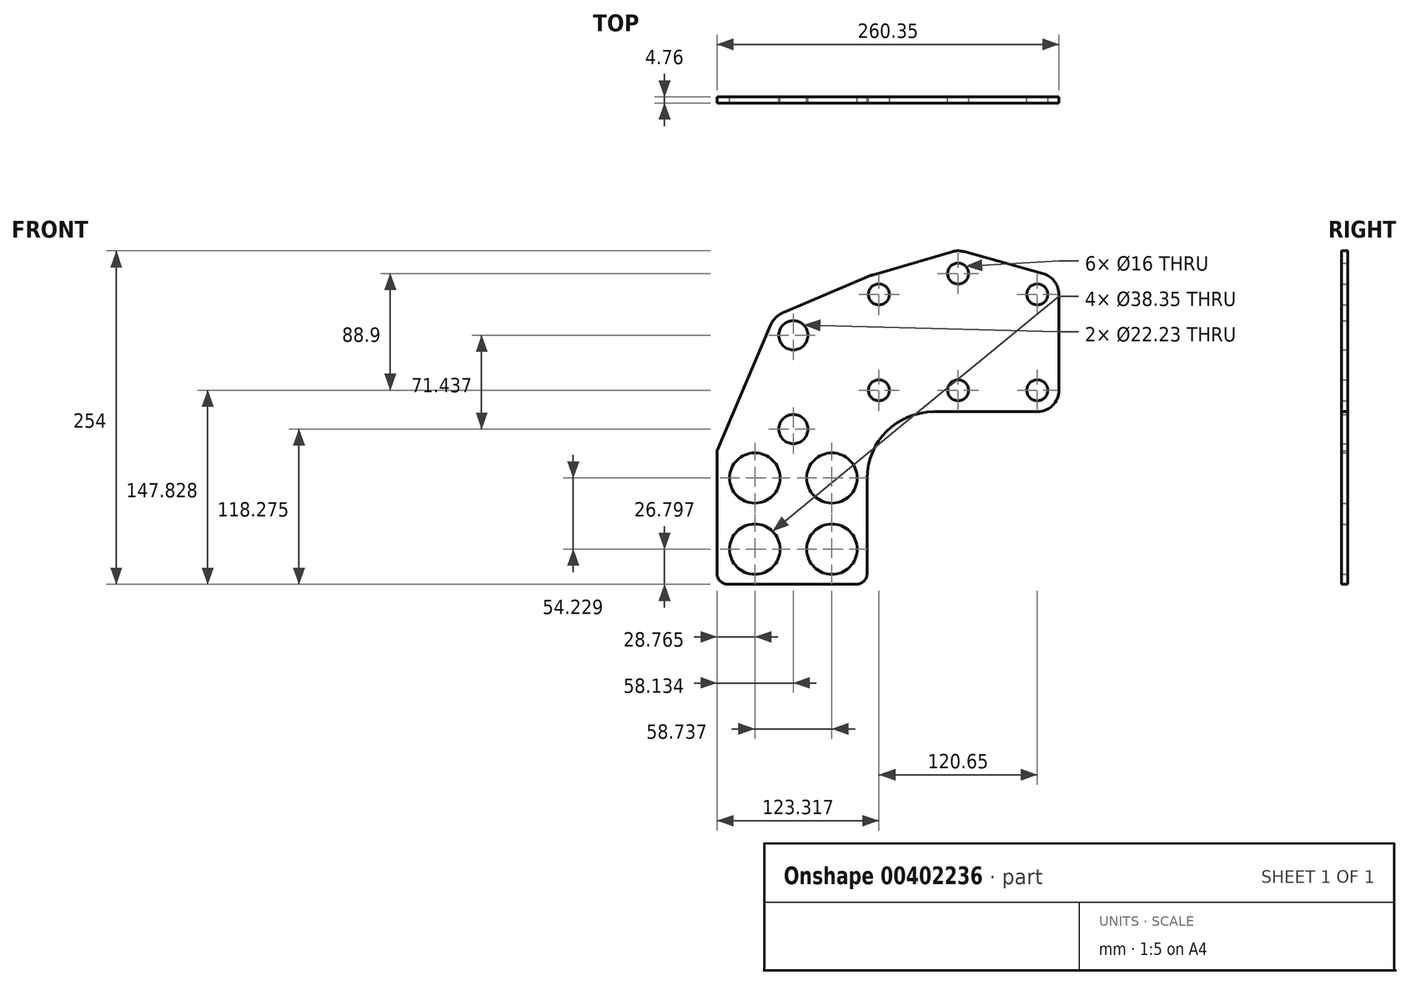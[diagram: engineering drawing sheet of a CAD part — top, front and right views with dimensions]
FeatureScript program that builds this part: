
annotation { "Feature Type Name" : "Feature", "Feature Type Description" : "" }
export const myFeature = defineFeature(function(context is Context, id is Id, definition is map)
    precondition{}
    {
        {
            var Q0;
            Q0=qCreatedBy(makeId("Front.planeOp"),FACE);
            var sketch = newSketch(context, id + "F0", { "sketchPlane" : qUnion([Q0])});
            skLineSegment(sketch, "E0.bottom", {"start": v(8.38, 0) * mm, "end": v(105.92, 0) * mm});
            skLineSegment(sketch, "E0.top", {"start": v(0, 254) * mm, "end": v(183.64, 254) * mm});
            skLineSegment(sketch, "E0.left", {"start": v(0, 8.38) * mm, "end": v(0, 101.6) * mm});
            skLineSegment(sketch, "E0.right", {"start": v(260.35, 0) * mm, "end": v(260.35, 131.45) * mm});
            skLineSegment(sketch, "E1", {"start": v(114.3, 8.38) * mm, "end": v(114.3, 80.64) * mm});
            skLineSegment(sketch, "E2", {"start": v(243.97, 131.45) * mm, "end": v(165.1, 131.45) * mm});
            skCircle(sketch, "E3", {"center": v(28.77, 26.8) * mm, "radius": 19.18 * mm});
            skCircle(sketch, "E4", {"center": v(87.5, 26.8) * mm, "radius": 19.18 * mm});
            skCircle(sketch, "E5", {"center": v(28.77, 81.03) * mm, "radius": 19.18 * mm});
            skCircle(sketch, "E6", {"center": v(87.5, 81.03) * mm, "radius": 19.18 * mm});
            skCircle(sketch, "E7", {"center": v(243.97, 147.83) * mm, "radius": 8 * mm});
            skCircle(sketch, "E8", {"center": v(243.97, 220.85) * mm, "radius": 8 * mm});
            skCircle(sketch, "E9", {"center": v(183.64, 147.83) * mm, "radius": 8 * mm});
            skCircle(sketch, "E10", {"center": v(183.64, 236.73) * mm, "radius": 8 * mm});
            skCircle(sketch, "E11", {"center": v(123.32, 147.83) * mm, "radius": 8 * mm});
            skCircle(sketch, "E12", {"center": v(123.32, 220.85) * mm, "radius": 8 * mm});
            skCircle(sketch, "E13", {"center": v(58.13, 189.71) * mm, "radius": 11.11 * mm});
            skCircle(sketch, "E14", {"center": v(58.13, 118.28) * mm, "radius": 11.11 * mm});
            skArc(sketch, "E15", {"start": v(188.28, 253.37) * mm, "mid": v(183.54, 254) * mm, "end": v(178.8, 253.3) * mm});
            skArc(sketch, "E16", {"start": v(50.75, 207.29) * mm, "mid": v(44.68, 203.22) * mm, "end": v(40.59, 197.16) * mm});
            skLineSegment(sketch, "E17", {"start": v(0, 101.6) * mm, "end": v(40.59, 197.16) * mm});
            skArc(sketch, "E18", {"start": v(260.35, 220.85) * mm, "mid": v(257.01, 230.76) * mm, "end": v(248.36, 236.64) * mm});
            skArc(sketch, "E19", {"start": v(243.97, 131.45) * mm, "mid": v(255.55, 136.24) * mm, "end": v(260.35, 147.83) * mm});
            skArc(sketch, "E20.filletArc", {"start": v(105.92, 0) * mm, "mid": v(111.84, 2.46) * mm, "end": v(114.3, 8.38) * mm});
            skPoint(sketch, "E21.visualSharp", {"position": v(0, 0) * mm});
            skArc(sketch, "E21.filletArc", {"start": v(0, 8.38) * mm, "mid": v(2.46, 2.46) * mm, "end": v(8.38, 0) * mm});
            skLineSegment(sketch, "E22.trimOffspring", {"start": v(260.35, 147.83) * mm, "end": v(260.35, 220.85) * mm});
            skLineSegment(sketch, "E23.trimOffspring", {"start": v(188.28, 253.37) * mm, "end": v(248.36, 236.64) * mm});
            skArc(sketch, "E24", {"start": v(118.94, 235.85) * mm, "mid": v(118.1, 235.58) * mm, "end": v(117.26, 235.25) * mm});
            skLineSegment(sketch, "E25", {"start": v(117.26, 235.25) * mm, "end": v(50.75, 207.29) * mm});
            skLineSegment(sketch, "E26", {"start": v(118.94, 235.85) * mm, "end": v(178.8, 253.3) * mm});
            skPoint(sketch, "E27.visualSharp", {"position": v(114.3, 131.45) * mm});
            skArc(sketch, "E27.filletArc", {"start": v(165.1, 131.44) * mm, "mid": v(129.18, 116.57) * mm, "end": v(114.3, 80.64) * mm});
            skSolve(sketch);
        }
        {
            var Q0;
            Q0=makeQuery(id+"F0.imprint","IMPRINT",FACE,{"disambiguationData":[TD([[makeQuery(id+"F0.imprint","IMPRINT",EDGE,{"derivedFrom":sQuery(id+"F0.wireOp",EDGE,"E0.bottom")}),1.0]])]});
            extrude(context, id + "F1", {"entities" : qUnion([Q0]), "depth" : 4.76 * mm});
        }
    });
